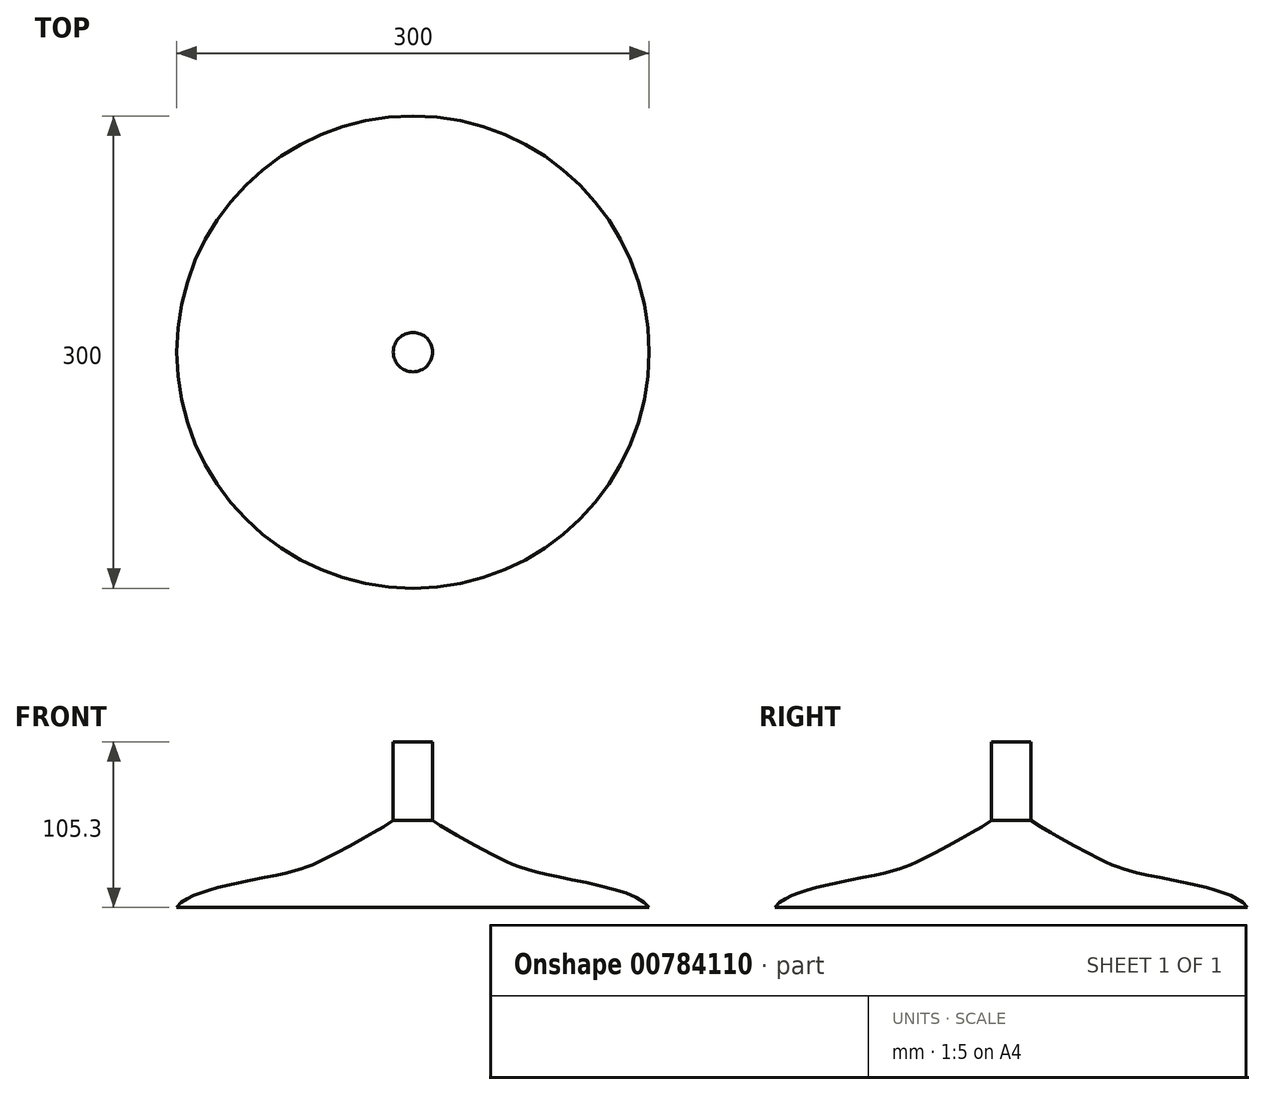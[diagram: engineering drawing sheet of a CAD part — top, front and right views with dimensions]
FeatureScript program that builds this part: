
annotation { "Feature Type Name" : "Feature", "Feature Type Description" : "" }
export const myFeature = defineFeature(function(context is Context, id is Id, definition is map)
    precondition{}
    {
        {
            var Q0;
            Q0=qCreatedBy(makeId("Front.planeOp"),FACE);
            var sketch = newSketch(context, id + "F0", { "sketchPlane" : qUnion([Q0])});
            skLineSegment(sketch, "E0", {"start": v(0, 0) * mm, "end": v(150, 0) * mm});
            skLineSegment(sketch, "E1", {"start": v(0, 55.3) * mm, "end": v(12.5, 55.3) * mm, "construction": true});
            skFitSpline(sketch, "E2", {"points": [v(12.5, 55.3) * mm, v(52.22, 32.81) * mm, v(83.46, 21.31) * mm, v(150, 0) * mm], "startDerivative": vector(103.55, -68.6) * mm, "endDerivative": vector(46.95, -83.5) * mm});
            skLineSegment(sketch, "E3", {"start": v(12.5, 55.3) * mm, "end": v(0, 55.3) * mm});
            skLineSegment(sketch, "E4", {"start": v(0, 55.3) * mm, "end": v(0, 0) * mm});
            skSolve(sketch);
        }
        {
            var Q0;
            Q0 = qSketchRegion(id + "F0", true);
            var Q1;
            Q1=sQuery(id+"F0.wireOp",EDGE,"E4");
            revolve(context, id + "F1", {"surfaceOperationType" : NewSurfaceOperationType.NEW, "entities" : qUnion([Q0]), "axis" : qUnion([Q1]), "revolveType" : RevolveType.FULL});
        }
        {
            var Q0;
            Q0=makeQuery(id+"F1.opRevolve","SWEPT_FACE",FACE,{"disambiguationData":[OSD([sQuery(id+"F0.wireOp",EDGE,"E3")])]});
            extrude(context, id + "F2", {"entities" : qUnion([Q0]), "operationType" : NewBodyOperationType.ADD, "depth" : 50 * mm, "offsetDistance" : 25 * mm});
        }
    });
